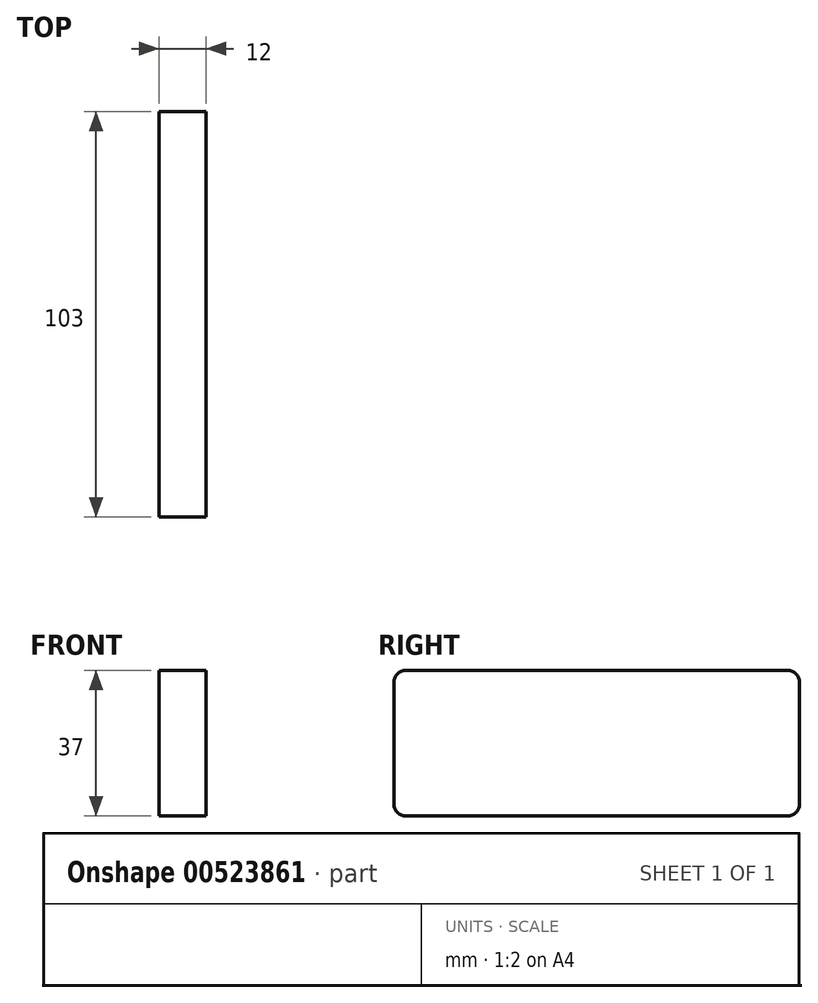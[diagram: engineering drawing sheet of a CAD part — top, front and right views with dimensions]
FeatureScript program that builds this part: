
annotation { "Feature Type Name" : "Feature", "Feature Type Description" : "" }
export const myFeature = defineFeature(function(context is Context, id is Id, definition is map)
    precondition{}
    {
        {
            var Q0;
            Q0=qCreatedBy(makeId("Right.planeOp"),FACE);
            var sketch = newSketch(context, id + "F0", { "sketchPlane" : qUnion([Q0])});
            skLineSegment(sketch, "E0.bottom", {"start": v(-51.5, 18.5) * mm, "end": v(51.5, 18.5) * mm});
            skLineSegment(sketch, "E0.top", {"start": v(-51.5, -18.5) * mm, "end": v(51.5, -18.5) * mm});
            skLineSegment(sketch, "E0.left", {"start": v(-51.5, 18.5) * mm, "end": v(-51.5, -18.5) * mm});
            skLineSegment(sketch, "E0.right", {"start": v(51.5, 18.5) * mm, "end": v(51.5, -18.5) * mm});
            skPoint(sketch, "E0.middle", {"position": v(0, 0) * mm});
            skSolve(sketch);
        }
        {
            var Q0;
            Q0=makeQuery(id+"F0.imprint","IMPRINT",FACE,{"disambiguationData":[TD([[makeQuery(id+"F0.imprint","IMPRINT",EDGE,{"derivedFrom":sQuery(id+"F0.wireOp",EDGE,"E0.bottom")}),-1.0]])]});
            extrude(context, id + "F1", {"entities" : qUnion([Q0]), "endBound" : BoundingType.SYMMETRIC, "depth" : 12 * mm, "offsetDistance" : 25 * mm});
        }
        {
            var Q0;
            Q0=makeQuery(id+"F1.opExtrude","SWEPT_EDGE",EDGE,{"disambiguationData":[OSD([sQuery(id+"F0.wireOp",EDGE,"E0.bottom"),sQuery(id+"F0.wireOp",EDGE,"E0.left")])]});
            var Q1;
            Q1=makeQuery(id+"F1.opExtrude","SWEPT_EDGE",EDGE,{"disambiguationData":[OSD([sQuery(id+"F0.wireOp",EDGE,"E0.top"),sQuery(id+"F0.wireOp",EDGE,"E0.left")])]});
            var Q2;
            Q2=makeQuery(id+"F1.opExtrude","SWEPT_EDGE",EDGE,{"disambiguationData":[OSD([sQuery(id+"F0.wireOp",EDGE,"E0.top"),sQuery(id+"F0.wireOp",EDGE,"E0.right")])]});
            var Q3;
            Q3=makeQuery(id+"F1.opExtrude","SWEPT_EDGE",EDGE,{"disambiguationData":[OSD([sQuery(id+"F0.wireOp",EDGE,"E0.bottom"),sQuery(id+"F0.wireOp",EDGE,"E0.right")])]});
            fillet(context, id + "F2", {"entities" : qUnion([Q0, Q1, Q2, Q3]), "radius" : 3 * mm, "tangentPropagation" : true, "allowEdgeOverflow" : false});
        }
    });
